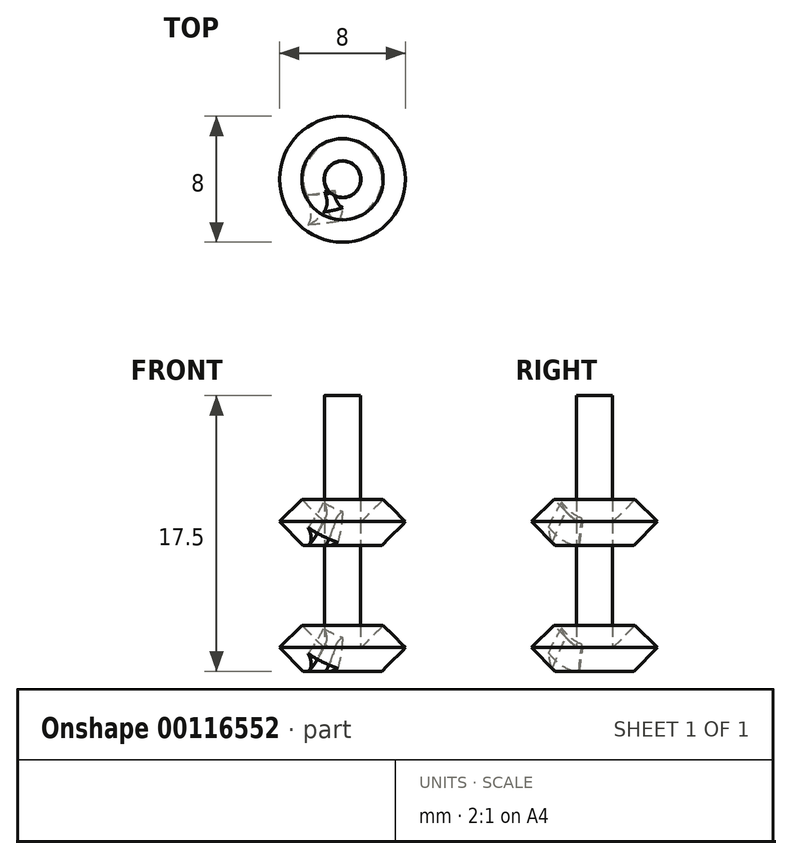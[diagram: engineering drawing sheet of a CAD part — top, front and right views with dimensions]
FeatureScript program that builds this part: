
annotation { "Feature Type Name" : "Feature", "Feature Type Description" : "" }
export const myFeature = defineFeature(function(context is Context, id is Id, definition is map)
    precondition{}
    {
        {
            var Q0;
            Q0=qCreatedBy(makeId("Front.planeOp"),FACE);
            var sketch = newSketch(context, id + "F0", { "sketchPlane" : qUnion([Q0])});
            skLineSegment(sketch, "E0", {"start": v(0, 0) * mm, "end": v(-1.17, 0) * mm});
            skLineSegment(sketch, "E1", {"start": v(-1.17, 0) * mm, "end": v(-2.59, 1.41) * mm});
            skLineSegment(sketch, "E2", {"start": v(-2.59, 1.41) * mm, "end": v(-4, 0) * mm});
            skLineSegment(sketch, "E3", {"start": v(-4, 0) * mm, "end": v(-2.5, -1.5) * mm});
            skLineSegment(sketch, "E4", {"start": v(-2.5, -1.5) * mm, "end": v(0, -1.5) * mm});
            skLineSegment(sketch, "E5", {"start": v(0, 0) * mm, "end": v(0, -1.5) * mm});
            skSolve(sketch);
        }
        {
            var Q0;
            Q0=makeQuery(id+"F0.imprint","IMPRINT",FACE,{"disambiguationData":[TD([[makeQuery(id+"F0.imprint","IMPRINT",EDGE,{"derivedFrom":sQuery(id+"F0.wireOp",EDGE,"E0")}),1.0]])]});
            var Q1;
            Q1=sQuery(id+"F0.wireOp",EDGE,"E5");
            revolve(context, id + "F1", {"entities" : qUnion([Q0]), "axis" : qUnion([Q1]), "revolveType" : RevolveType.FULL});
        }
        {
            var Q0;
            Q0=qCreatedBy(makeId("Front.planeOp"),FACE);
            var sketch = newSketch(context, id + "F2", { "sketchPlane" : qUnion([Q0])});
            skLineSegment(sketch, "E6", {"start": v(0, 0) * mm, "end": v(0, 4) * mm, "construction": true});
            skLineSegment(sketch, "E7", {"start": v(0, 4) * mm, "end": v(-4, 0) * mm, "construction": true});
            skLineSegment(sketch, "E8", {"start": v(-4, 0) * mm, "end": v(-2.48, -1.52) * mm, "construction": true});
            skSolve(sketch);
        }
        {
            var Q0;
            Q0=sQuery(id+"F2.wireOp",EDGE,"E8");
            cPlane(context, id + "F3", {"entities" : qUnion([Q0]), "cplaneType" : CPlaneType.LINE_ANGLE, "offset" : 25 * mm, "angle" : 90 * degree, "width" : 150 * mm, "height" : 150 * mm});
        }
        {
            var Q0;
            Q0=qCreatedBy(id+"F3.planeOp",FACE);
            var sketch = newSketch(context, id + "F4", { "sketchPlane" : qUnion([Q0])});
            skLineSegment(sketch, "E9", {"start": v(-0.98, 0) * mm, "end": v(-0.98, 0.5) * mm});
            skArc(sketch, "E10", {"start": v(-3.03, 1.2) * mm, "mid": v(-2.1, 0.57) * mm, "end": v(-0.98, 0.5) * mm});
            skLineSegment(sketch, "E11", {"start": v(-3.03, 1.2) * mm, "end": v(-3.03, 0) * mm});
            skLineSegment(sketch, "E12", {"start": v(-3.03, 0) * mm, "end": v(-0.98, 0) * mm});
            skLineSegment(sketch, "E13.MirrorCS", {"start": v(-3.03, -1.2) * mm, "end": v(-3.03, 0) * mm});
            skArc(sketch, "E14.MirrorCS", {"start": v(-3.03, -1.2) * mm, "mid": v(-2.1, -0.57) * mm, "end": v(-0.98, -0.5) * mm});
            skLineSegment(sketch, "E15.MirrorCS", {"start": v(-0.98, 0) * mm, "end": v(-0.98, -0.5) * mm});
            skSolve(sketch);
        }
        {
            var Q0;
            Q0=qSketchRegion(id+"F4",true);
            var Q1;
            Q1=sQuery(id+"F2.wireOp",VERTEX,"E7.start");
            loft(context, id + "F5", {"operationType" : NewBodyOperationType.REMOVE, "startCondition" : LoftEndDerivativeType.NORMAL_TO_PROFILE, "startMagnitude" : 1, "sheetProfilesArray" : [{ "sheetProfileEntities" : qUnion([Q0]) }, { "sheetProfileEntities" : qUnion([Q1]) }]});
        }
        {
            var Q0;
            Q0=makeQuery(id+"F1.opRevolve","SWEPT_FACE",FACE,{"disambiguationData":[OSD([sQuery(id+"F0.wireOp",EDGE,"E0")])]});
            var sketch = newSketch(context, id + "F6", { "sketchPlane" : qUnion([Q0])});
            skCircle(sketch, "E16", {"center": v(0, 0) * mm, "radius": 1.15 * mm});
            skSolve(sketch);
        }
        {
            var Q0;
            Q0 = qSketchRegion(id + "F6", true);
            extrude(context, id + "F7", {"entities" : qUnion([Q0]), "operationType" : NewBodyOperationType.ADD, "depth" : 8 * mm});
        }
        {
            var Q0;
            Q0=makeQuery(id+"F1.opRevolve","SWEPT_BODY",BODY,{"disambiguationData":[OSD([sQuery(id+"F0.wireOp",EDGE,"E0"),sQuery(id+"F0.wireOp",EDGE,"E1"),sQuery(id+"F0.wireOp",EDGE,"E2"),sQuery(id+"F0.wireOp",EDGE,"E3"),sQuery(id+"F0.wireOp",EDGE,"E4"),sQuery(id+"F0.wireOp",EDGE,"E5")])]});
            transform(context, id + "F8", {"entities" : qUnion([Q0]), "transformType" : TransformType.TRANSLATION_3D, "dx" : 0 * mm, "dy" : 0 * mm, "dz" : 8 * mm, "makeCopy" : true});
        }
    });
